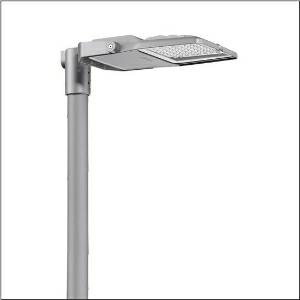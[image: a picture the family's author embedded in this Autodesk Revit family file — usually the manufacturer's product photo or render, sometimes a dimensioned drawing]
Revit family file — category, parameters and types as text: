
# Revit family: floodlight_fl_21_mini___pl52_5xa7776b2d3a_5eef
name_source: partatom
category: Lighting Fixtures
units: mm (PartAtom-declared; Revit-internal decimal feet)

## family parameters
Cut with Voids When Loaded = No
Host = Face
Light Source = No
Part Type = Normal
Room Calculation Point = No
Round Connector Dimension = Use Diameter
Shared = No

## types (1)
- --- (1 x LED, 6230 lm, 45.7 W, 3000K)
    Apparent Load = 46 VA
    CIE Flux Codes = 26 60 98 100 100
    Color Rendering = 70
    Color Temperature = 3000K
    Default Elevation = 1800 mm
    Description = Floodlight FL 21 mini, floodlight, primary light control with lens, of PMMA, primary optical cover: protective disc, of toughened safety glass, transparent, light distribution: PL52, light emission: direct distribution, installation type: surface-mounted, LED, High Power LED, rated luminous flux: 6.230lm, luminous efficacy: 136lm/W, light colour: 730, colour temperature: 3000K, control gear: Smart Interface (Zhaga), control: flexible luminous flux parameterisation, time-dependent luminous flux control, constant luminous flux control, overheat protection, pre-setting: logarithmic dimming characteristic, with terminal, 6-pole, mains connection: 220..240V, AC, 50/60Hz, start of lifetime: 46W, end of service life: 48W, reduction: 22W, luminaire housing, of diecast aluminium, powder-coated, SITECO metallic grey (DB 702S), corrosivity category C5 mid according to DIN EN ISO 12944, suitable for swimming pools, chlorine-resistant, sealing non-destructively replaceable, please order mast flange separately, mast bracket, of steel, galvanised, powder-coated, SITECO metallic grey (DB 702S), Smart Interface below and above, protection rating (complete): IP66, insulation class (complete): insulation class II (safety insulation), certification: CE, ENEC, VDE, protection symbol: D, impact resistance: IK08, permissible operating ambient temperature: -40..+40°C, permissible operating ambient temperature for outdoor applications: -40..+50°C, standard: DIN EN 12944, LABS conformity tested according to VDMA 24364:2018-05, packaging unit: 1 piece

Light Distribution: PL52
    Height = 70 mm
    Lamp = 1 x LED
    Lamp Light Flux = 6230 lm
    Lamp Power = 45.7 W
    Lamp count = 1
    Length = 485 mm
    Luminous efficacy = 136 lm/W
    Manufacturer = Siteco
    ModVariant = No
    Model = 5XA7776B2D3A
    Number of Poles = 1
    OnlyDefault = Yes
    Power Factor = 1
    Product Name = Floodlight FL 21 mini | PL52
    Product group = floodlight | pylon annexe
    ProductGroupID = 6201
    Protection Class = Protection class II
    Protection Degree = IP 66
    RLX_Detail_Level = 1
    RLX_Emergency_Light_Flux = 0 lm
    RLX_Emergency_Type = 0
    RLX_Emergency_Type_DB = No
    RlxData = <blob elided: 101369 chars, md5=772bbe7d>
    Socket = socket
    Standby Power = 0 W
    System Light Flux = 6230 lm
    System Power = 46 W
    Type Comments = factory setting: luminous flux: 100 % | dim-lin: 254 | 463 mA
    Type Image = l_1007125.jpg
    URL = http://relux.com
    VarID = @adj_162855
    Voltage = 0 V
    Weight = 0.00 kg
    Width = 337 mm

## geometry (parser evidence)
native form markers: Blend x4, Sweep x12
no freeform markers — native parametric forms only
